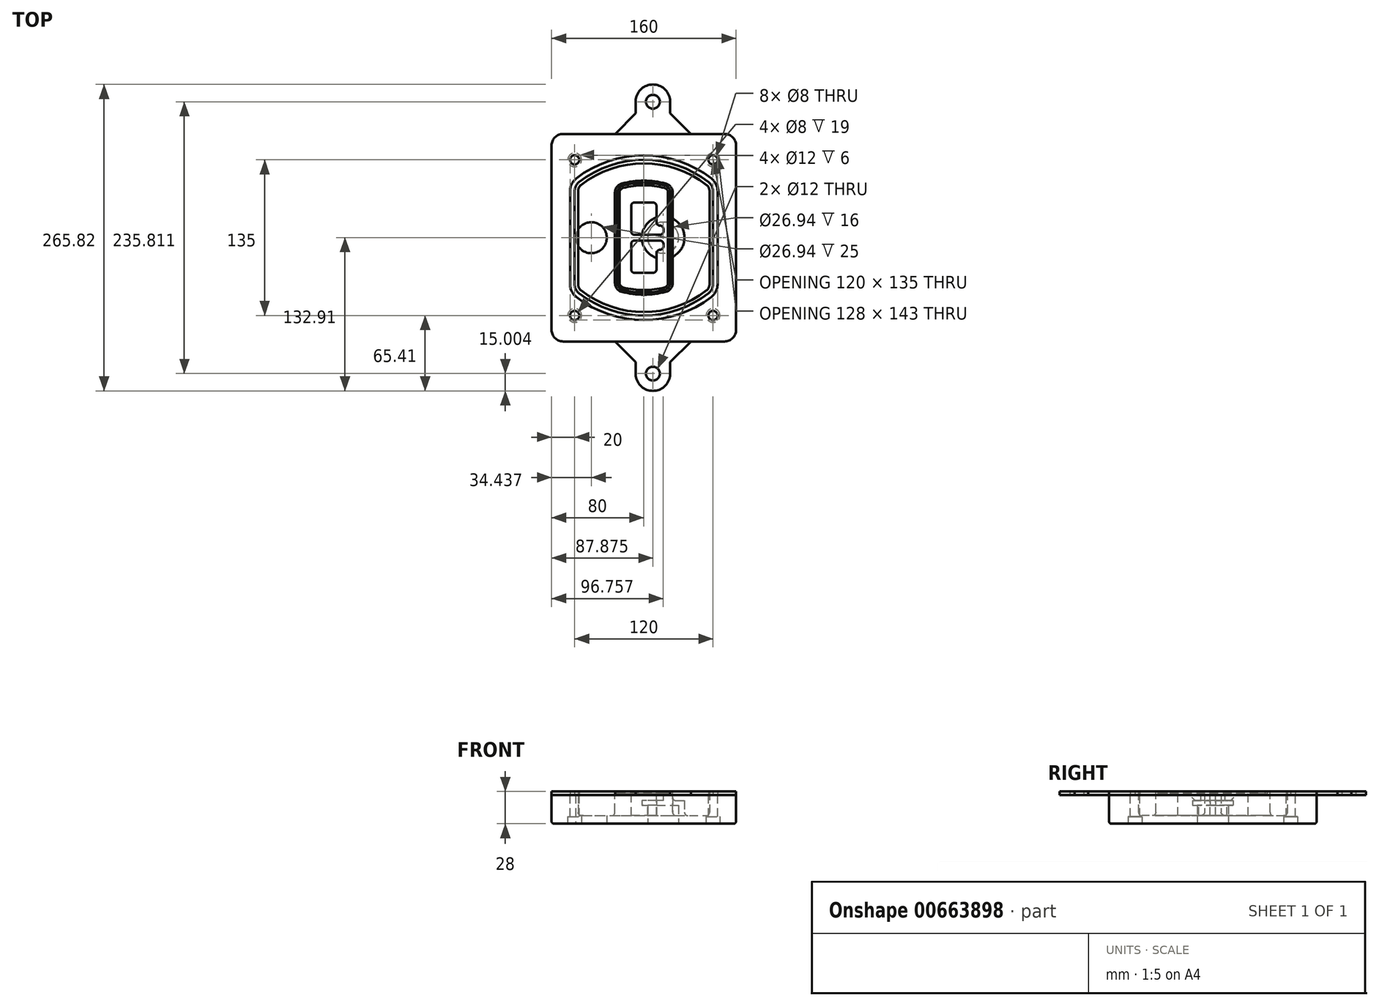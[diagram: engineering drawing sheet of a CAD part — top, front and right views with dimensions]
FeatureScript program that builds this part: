
annotation { "Feature Type Name" : "Feature", "Feature Type Description" : "" }
export const myFeature = defineFeature(function(context is Context, id is Id, definition is map)
    precondition{}
    {
        {
            var Q0;
            Q0=qCreatedBy(makeId("Top.planeOp"),FACE);
            var sketch = newSketch(context, id + "F0", { "sketchPlane" : qUnion([Q0])});
            skPoint(sketch, "E0.rect.middle", {"position": v(0, 0) * mm});
            skLineSegment(sketch, "E1.bottom", {"start": v(-70, -90) * mm, "end": v(70, -90) * mm});
            skLineSegment(sketch, "E1.top", {"start": v(-70, 90) * mm, "end": v(70, 90) * mm});
            skLineSegment(sketch, "E1.left", {"start": v(-80, -80) * mm, "end": v(-80, 80) * mm});
            skLineSegment(sketch, "E1.right", {"start": v(80, -80) * mm, "end": v(80, 80) * mm});
            skLineSegment(sketch, "E2", {"start": v(-80, 90) * mm, "end": v(80, -90) * mm, "construction": true});
            skLineSegment(sketch, "E3", {"start": v(80, 90) * mm, "end": v(-80, -90) * mm, "construction": true});
            skCircle(sketch, "E4", {"center": v(-60, 67.5) * mm, "radius": 4 * mm});
            skCircle(sketch, "E5", {"center": v(60, 67.5) * mm, "radius": 4 * mm});
            skCircle(sketch, "E6", {"center": v(60, -67.5) * mm, "radius": 4 * mm});
            skCircle(sketch, "E7", {"center": v(-60, -67.5) * mm, "radius": 4 * mm});
            skLineSegment(sketch, "E8", {"start": v(-60, 67.5) * mm, "end": v(60, 67.5) * mm, "construction": true});
            skLineSegment(sketch, "E9", {"start": v(60, 67.5) * mm, "end": v(60, -67.5) * mm, "construction": true});
            skLineSegment(sketch, "E10", {"start": v(60, -67.5) * mm, "end": v(-60, -67.5) * mm, "construction": true});
            skLineSegment(sketch, "E11", {"start": v(-60, -67.5) * mm, "end": v(-60, 67.5) * mm, "construction": true});
            skLineSegment(sketch, "E12", {"start": v(-60, 40.3) * mm, "end": v(-60, -40.3) * mm});
            skLineSegment(sketch, "E13", {"start": v(60, 40.3) * mm, "end": v(60, -40.3) * mm});
            skArc(sketch, "E14", {"start": v(56.15, 48.18) * mm, "mid": v(0, 67.5) * mm, "end": v(-56.15, 48.18) * mm});
            skArc(sketch, "E15", {"start": v(-56.15, -48.18) * mm, "mid": v(0, -67.5) * mm, "end": v(56.15, -48.18) * mm});
            skLineSegment(sketch, "E16", {"start": v(-60, 0) * mm, "end": v(60, 0) * mm, "construction": true});
            skPoint(sketch, "E17.visualSharp", {"position": v(-60, -45) * mm});
            skArc(sketch, "E17.filletArc", {"start": v(-60, -40.3) * mm, "mid": v(-58.99, -44.68) * mm, "end": v(-56.15, -48.18) * mm});
            skPoint(sketch, "E18.visualSharp", {"position": v(-60, 45) * mm});
            skArc(sketch, "E18.filletArc", {"start": v(-56.15, 48.18) * mm, "mid": v(-58.99, 44.68) * mm, "end": v(-60, 40.3) * mm});
            skPoint(sketch, "E19.visualSharp", {"position": v(60, 45) * mm});
            skArc(sketch, "E19.filletArc", {"start": v(60, 40.3) * mm, "mid": v(58.99, 44.68) * mm, "end": v(56.15, 48.18) * mm});
            skPoint(sketch, "E20.visualSharp", {"position": v(60, -45) * mm});
            skArc(sketch, "E20.filletArc", {"start": v(56.15, -48.18) * mm, "mid": v(58.99, -44.68) * mm, "end": v(60, -40.3) * mm});
            skPoint(sketch, "E21.visualSharp", {"position": v(-80, 90) * mm});
            skArc(sketch, "E21.filletArc", {"start": v(-70, 90) * mm, "mid": v(-77.07, 87.07) * mm, "end": v(-80, 80) * mm});
            skPoint(sketch, "E22.visualSharp", {"position": v(80, 90) * mm});
            skArc(sketch, "E22.filletArc", {"start": v(80, 80) * mm, "mid": v(77.07, 87.07) * mm, "end": v(70, 90) * mm});
            skPoint(sketch, "E23.visualSharp", {"position": v(80, -90) * mm});
            skArc(sketch, "E23.filletArc", {"start": v(70, -90) * mm, "mid": v(77.07, -87.07) * mm, "end": v(80, -80) * mm});
            skPoint(sketch, "E24.visualSharp", {"position": v(-80, -90) * mm});
            skArc(sketch, "E24.filletArc", {"start": v(-80, -80) * mm, "mid": v(-77.07, -87.07) * mm, "end": v(-70, -90) * mm});
            skArc(sketch, "E25.0", {"start": v(57, 40.3) * mm, "mid": v(56.3, 43.36) * mm, "end": v(54.3, 45.81) * mm});
            skLineSegment(sketch, "E25.1", {"start": v(57, 40.3) * mm, "end": v(57, -40.3) * mm});
            skArc(sketch, "E25.2", {"start": v(54.3, -45.81) * mm, "mid": v(56.3, -43.36) * mm, "end": v(57, -40.3) * mm});
            skArc(sketch, "E25.3", {"start": v(-54.3, -45.81) * mm, "mid": v(0, -64.5) * mm, "end": v(54.3, -45.81) * mm});
            skArc(sketch, "E25.4", {"start": v(-57, -40.3) * mm, "mid": v(-56.3, -43.36) * mm, "end": v(-54.3, -45.81) * mm});
            skArc(sketch, "E25.5", {"start": v(54.3, 45.81) * mm, "mid": v(0, 64.5) * mm, "end": v(-54.3, 45.81) * mm});
            skLineSegment(sketch, "E25.6", {"start": v(-57, 40.3) * mm, "end": v(-57, -40.3) * mm});
            skArc(sketch, "E25.7", {"start": v(-54.3, 45.81) * mm, "mid": v(-56.3, 43.36) * mm, "end": v(-57, 40.3) * mm});
            skArc(sketch, "E26.0", {"start": v(-58.62, 51.33) * mm, "mid": v(-62.58, 46.43) * mm, "end": v(-64, 40.3) * mm});
            skArc(sketch, "E26.1", {"start": v(58.62, 51.33) * mm, "mid": v(0, 71.5) * mm, "end": v(-58.62, 51.33) * mm});
            skArc(sketch, "E26.2", {"start": v(64, 40.3) * mm, "mid": v(62.58, 46.43) * mm, "end": v(58.62, 51.33) * mm});
            skLineSegment(sketch, "E26.3", {"start": v(64, 40.3) * mm, "end": v(64, -40.3) * mm});
            skArc(sketch, "E26.4", {"start": v(58.62, -51.33) * mm, "mid": v(62.58, -46.43) * mm, "end": v(64, -40.3) * mm});
            skLineSegment(sketch, "E26.5", {"start": v(-64, 40.3) * mm, "end": v(-64, -40.3) * mm});
            skArc(sketch, "E26.6", {"start": v(-58.62, -51.33) * mm, "mid": v(0, -71.5) * mm, "end": v(58.62, -51.33) * mm});
            skArc(sketch, "E26.7", {"start": v(-64, -40.3) * mm, "mid": v(-62.58, -46.43) * mm, "end": v(-58.62, -51.33) * mm});
            skSolve(sketch);
        }
        {
            var Q0;
            Q0=makeQuery(id+"F0.imprint","IMPRINT",FACE,{"disambiguationData":[TD([[makeQuery(id+"F0.imprint","IMPRINT",EDGE,{"derivedFrom":sQuery(id+"F0.wireOp",EDGE,"E1.bottom")}),1.0]])]});
            var Q1;
            Q1=makeQuery(id+"F0.imprint","IMPRINT",FACE,{"disambiguationData":[TD([[makeQuery(id+"F0.imprint","IMPRINT",EDGE,{"derivedFrom":sQuery(id+"F0.wireOp",EDGE,"E12")}),1.0]])]});
            var Q2;
            Q2=makeQuery(id+"F0.imprint","IMPRINT",FACE,{"disambiguationData":[TD([[makeQuery(id+"F0.imprint","IMPRINT",EDGE,{"derivedFrom":sQuery(id+"F0.wireOp",EDGE,"E25.0")}),1.0]])]});
            var Q3;
            Q3=makeQuery(id+"F0.imprint","IMPRINT",FACE,{"disambiguationData":[TD([[makeQuery(id+"F0.imprint","IMPRINT",EDGE,{"derivedFrom":sQuery(id+"F0.wireOp",EDGE,"E12")}),-1.0]])]});
            extrude(context, id + "F1", {"entities" : qUnion([Q0, Q1, Q2, Q3]), "oppositeDirection" : true, "depth" : 25 * mm});
        }
        {
            var Q0;
            Q0=makeQuery(id+"F0.imprint","IMPRINT",FACE,{"disambiguationData":[TD([[makeQuery(id+"F0.imprint","IMPRINT",EDGE,{"derivedFrom":sQuery(id+"F0.wireOp",EDGE,"E12")}),1.0]])]});
            extrude(context, id + "F2", {"entities" : qUnion([Q0]), "operationType" : NewBodyOperationType.ADD, "depth" : 3 * mm});
        }
        {
            var Q0;
            Q0=makeQuery(id+"F0.imprint","IMPRINT",FACE,{"disambiguationData":[TD([[makeQuery(id+"F0.imprint","IMPRINT",EDGE,{"derivedFrom":sQuery(id+"F0.wireOp",EDGE,"E25.0")}),1.0]])]});
            extrude(context, id + "F3", {"entities" : qUnion([Q0]), "operationType" : NewBodyOperationType.REMOVE, "oppositeDirection" : true, "depth" : 18 * mm});
        }
        {
            var Q0;
            Q0=makeQuery(id+"F2.opExtrude","CAP_FACE",FACE,{"disambiguationData":[OSD([sQuery(id+"F0.wireOp",EDGE,"E12"),sQuery(id+"F0.wireOp",EDGE,"E13"),sQuery(id+"F0.wireOp",EDGE,"E14"),sQuery(id+"F0.wireOp",EDGE,"E15"),sQuery(id+"F0.wireOp",EDGE,"E17.filletArc"),sQuery(id+"F0.wireOp",EDGE,"E18.filletArc"),sQuery(id+"F0.wireOp",EDGE,"E19.filletArc"),sQuery(id+"F0.wireOp",EDGE,"E20.filletArc"),sQuery(id+"F0.wireOp",EDGE,"E25.0"),sQuery(id+"F0.wireOp",EDGE,"E25.1"),sQuery(id+"F0.wireOp",EDGE,"E25.2"),sQuery(id+"F0.wireOp",EDGE,"E25.3"),sQuery(id+"F0.wireOp",EDGE,"E25.4"),sQuery(id+"F0.wireOp",EDGE,"E25.5"),sQuery(id+"F0.wireOp",EDGE,"E25.6"),sQuery(id+"F0.wireOp",EDGE,"E25.7")])],"isStart":false});
            var sketch = newSketch(context, id + "F4", { "sketchPlane" : qUnion([Q0])});
            skArc(sketch, "E27.0", {"start": v(-19.08, -46.97) * mm, "mid": v(0, -49.5) * mm, "end": v(19.08, -46.97) * mm});
            skArc(sketch, "E28.0", {"start": v(19.08, 46.97) * mm, "mid": v(0, 49.5) * mm, "end": v(-19.08, 46.97) * mm});
            skLineSegment(sketch, "E29", {"start": v(-25, 39.25) * mm, "end": v(-25, -39.25) * mm});
            skLineSegment(sketch, "E30", {"start": v(25, 39.25) * mm, "end": v(25, -39.25) * mm});
            skLineSegment(sketch, "E31", {"start": v(-25, 45.1) * mm, "end": v(25, 45.1) * mm, "construction": true});
            skLineSegment(sketch, "E32", {"start": v(-25, -45.1) * mm, "end": v(25, -45.1) * mm, "construction": true});
            skPoint(sketch, "E33.visualSharp", {"position": v(-25, 45.1) * mm});
            skArc(sketch, "E33.filletArc", {"start": v(-19.08, 46.97) * mm, "mid": v(-23.35, 44.11) * mm, "end": v(-25, 39.25) * mm});
            skPoint(sketch, "E34.visualSharp", {"position": v(25, 45.1) * mm});
            skArc(sketch, "E34.filletArc", {"start": v(25, 39.25) * mm, "mid": v(23.35, 44.11) * mm, "end": v(19.08, 46.97) * mm});
            skPoint(sketch, "E35.visualSharp", {"position": v(25, -45.1) * mm});
            skArc(sketch, "E35.filletArc", {"start": v(19.08, -46.97) * mm, "mid": v(23.35, -44.11) * mm, "end": v(25, -39.25) * mm});
            skPoint(sketch, "E36.visualSharp", {"position": v(-25, -45.1) * mm});
            skArc(sketch, "E36.filletArc", {"start": v(-25, -39.25) * mm, "mid": v(-23.35, -44.11) * mm, "end": v(-19.08, -46.97) * mm});
            skArc(sketch, "E37.0", {"start": v(54.3, 45.81) * mm, "mid": v(0, 64.5) * mm, "end": v(-54.3, 45.81) * mm});
            skArc(sketch, "E37.1", {"start": v(-54.3, 45.81) * mm, "mid": v(-56.3, 43.36) * mm, "end": v(-57, 40.3) * mm});
            skLineSegment(sketch, "E37.2", {"start": v(-57, 40.3) * mm, "end": v(-57, -40.3) * mm});
            skArc(sketch, "E37.3", {"start": v(-57, -40.3) * mm, "mid": v(-56.3, -43.36) * mm, "end": v(-54.3, -45.81) * mm});
            skArc(sketch, "E37.4", {"start": v(-54.3, -45.81) * mm, "mid": v(0, -64.5) * mm, "end": v(54.3, -45.81) * mm});
            skArc(sketch, "E37.5", {"start": v(54.3, -45.81) * mm, "mid": v(56.3, -43.36) * mm, "end": v(57, -40.3) * mm});
            skLineSegment(sketch, "E37.6", {"start": v(57, 40.3) * mm, "end": v(57, -40.3) * mm});
            skArc(sketch, "E37.7", {"start": v(57, 40.3) * mm, "mid": v(56.3, 43.36) * mm, "end": v(54.3, 45.81) * mm});
            skLineSegment(sketch, "E38.0", {"start": v(23, 39.25) * mm, "end": v(23, -39.25) * mm});
            skArc(sketch, "E38.1", {"start": v(18.56, -45.04) * mm, "mid": v(21.76, -42.9) * mm, "end": v(23, -39.25) * mm});
            skArc(sketch, "E38.2", {"start": v(-18.56, -45.04) * mm, "mid": v(0, -47.5) * mm, "end": v(18.56, -45.04) * mm});
            skArc(sketch, "E38.3", {"start": v(-23, -39.25) * mm, "mid": v(-21.76, -42.9) * mm, "end": v(-18.56, -45.04) * mm});
            skLineSegment(sketch, "E38.4", {"start": v(-23, 39.25) * mm, "end": v(-23, -39.25) * mm});
            skArc(sketch, "E38.5", {"start": v(23, 39.25) * mm, "mid": v(21.76, 42.9) * mm, "end": v(18.56, 45.04) * mm});
            skArc(sketch, "E38.6", {"start": v(-18.56, 45.04) * mm, "mid": v(-21.76, 42.9) * mm, "end": v(-23, 39.25) * mm});
            skArc(sketch, "E38.7", {"start": v(18.56, 45.04) * mm, "mid": v(0, 47.5) * mm, "end": v(-18.56, 45.04) * mm});
            skArc(sketch, "E39.0", {"start": v(21, 39.25) * mm, "mid": v(20.18, 41.68) * mm, "end": v(18.04, 43.1) * mm});
            skLineSegment(sketch, "E39.1", {"start": v(21, 39.25) * mm, "end": v(21, -39.25) * mm});
            skArc(sketch, "E39.2", {"start": v(18.04, -43.1) * mm, "mid": v(20.18, -41.68) * mm, "end": v(21, -39.25) * mm});
            skArc(sketch, "E39.3", {"start": v(-18.04, -43.1) * mm, "mid": v(0, -45.5) * mm, "end": v(18.04, -43.1) * mm});
            skArc(sketch, "E39.4", {"start": v(-21, -39.25) * mm, "mid": v(-20.18, -41.68) * mm, "end": v(-18.04, -43.1) * mm});
            skArc(sketch, "E39.5", {"start": v(18.04, 43.1) * mm, "mid": v(0, 45.5) * mm, "end": v(-18.04, 43.1) * mm});
            skLineSegment(sketch, "E39.6", {"start": v(-21, 39.25) * mm, "end": v(-21, -39.25) * mm});
            skArc(sketch, "E39.7", {"start": v(-18.04, 43.1) * mm, "mid": v(-20.18, 41.68) * mm, "end": v(-21, 39.25) * mm});
            skLineSegment(sketch, "E40", {"start": v(-25, 0) * mm, "end": v(25, 0) * mm, "construction": true});
            skLineSegment(sketch, "E41", {"start": v(-11, 5.5) * mm, "end": v(-11, 27.5) * mm});
            skLineSegment(sketch, "E42", {"start": v(-8, 30.5) * mm, "end": v(8, 30.5) * mm});
            skLineSegment(sketch, "E43", {"start": v(11, 27.5) * mm, "end": v(11, 13.5) * mm});
            skLineSegment(sketch, "E44", {"start": v(14, 10.5) * mm, "end": v(14, 10.5) * mm});
            skLineSegment(sketch, "E45", {"start": v(17, 7.5) * mm, "end": v(17, 5.5) * mm});
            skLineSegment(sketch, "E46", {"start": v(14, 2.5) * mm, "end": v(-8, 2.5) * mm});
            skPoint(sketch, "E47.visualSharp", {"position": v(-11, 30.5) * mm});
            skArc(sketch, "E47.filletArc", {"start": v(-8, 30.5) * mm, "mid": v(-10.12, 29.62) * mm, "end": v(-11, 27.5) * mm});
            skPoint(sketch, "E48.visualSharp", {"position": v(11, 30.5) * mm});
            skArc(sketch, "E48.filletArc", {"start": v(11, 27.5) * mm, "mid": v(10.12, 29.62) * mm, "end": v(8, 30.5) * mm});
            skPoint(sketch, "E49.visualSharp", {"position": v(11, 10.5) * mm});
            skArc(sketch, "E49.filletArc", {"start": v(11, 13.5) * mm, "mid": v(11.88, 11.38) * mm, "end": v(14, 10.5) * mm});
            skPoint(sketch, "E50.visualSharp", {"position": v(17, 10.5) * mm});
            skArc(sketch, "E50.filletArc", {"start": v(17, 7.5) * mm, "mid": v(16.12, 9.62) * mm, "end": v(14, 10.5) * mm});
            skPoint(sketch, "E51.visualSharp", {"position": v(17, 2.5) * mm});
            skArc(sketch, "E51.filletArc", {"start": v(14, 2.5) * mm, "mid": v(16.12, 3.38) * mm, "end": v(17, 5.5) * mm});
            skPoint(sketch, "E52.visualSharp", {"position": v(-11, 2.5) * mm});
            skArc(sketch, "E52.filletArc", {"start": v(-11, 5.5) * mm, "mid": v(-10.12, 3.38) * mm, "end": v(-8, 2.5) * mm});
            skLineSegment(sketch, "E53.0.MirrorCS", {"start": v(14, -2.5) * mm, "end": v(-8, -2.5) * mm});
            skArc(sketch, "E54.0.MirrorCS", {"start": v(-11, -5.5) * mm, "mid": v(-10.12, -3.38) * mm, "end": v(-8, -2.5) * mm});
            skLineSegment(sketch, "E55.0.MirrorCS", {"start": v(-11, -5.5) * mm, "end": v(-11, -27.5) * mm});
            skArc(sketch, "E56.0.MirrorCS", {"start": v(-8, -30.5) * mm, "mid": v(-10.12, -29.62) * mm, "end": v(-11, -27.5) * mm});
            skLineSegment(sketch, "E57.0.MirrorCS", {"start": v(-8, -30.5) * mm, "end": v(8, -30.5) * mm});
            skArc(sketch, "E58.0.MirrorCS", {"start": v(11, -27.5) * mm, "mid": v(10.12, -29.62) * mm, "end": v(8, -30.5) * mm});
            skLineSegment(sketch, "E59.0.MirrorCS", {"start": v(11, -27.5) * mm, "end": v(11, -13.5) * mm});
            skArc(sketch, "E60.0.MirrorCS", {"start": v(11, -13.5) * mm, "mid": v(11.88, -11.38) * mm, "end": v(14, -10.5) * mm});
            skArc(sketch, "E61.0.MirrorCS", {"start": v(17, -7.5) * mm, "mid": v(16.12, -9.62) * mm, "end": v(14, -10.5) * mm});
            skLineSegment(sketch, "E62.0.MirrorCS", {"start": v(17, -7.5) * mm, "end": v(17, -5.5) * mm});
            skArc(sketch, "E63.0.MirrorCS", {"start": v(14, -2.5) * mm, "mid": v(16.12, -3.38) * mm, "end": v(17, -5.5) * mm});
            skSolve(sketch);
        }
        {
            var Q0;
            Q0=makeQuery(id+"F4.imprint","IMPRINT",FACE,{"disambiguationData":[TD([[makeQuery(id+"F4.imprint","IMPRINT",EDGE,{"derivedFrom":sQuery(id+"F4.wireOp",EDGE,"E27.0")}),1.0]])]});
            var Q1;
            Q1=makeQuery(id+"F4.imprint","IMPRINT",FACE,{"disambiguationData":[TD([[makeQuery(id+"F4.imprint","IMPRINT",EDGE,{"derivedFrom":sQuery(id+"F4.wireOp",EDGE,"E38.0")}),-1.0]])]});
            var Q2;
            Q2=makeQuery(id+"F4.imprint","IMPRINT",FACE,{"disambiguationData":[TD([[makeQuery(id+"F4.imprint","IMPRINT",EDGE,{"derivedFrom":sQuery(id+"F4.wireOp",EDGE,"E39.0")}),1.0]])]});
            extrude(context, id + "F5", {"entities" : qUnion([Q0, Q1, Q2]), "operationType" : NewBodyOperationType.ADD, "endBound" : BoundingType.UP_TO_NEXT, "oppositeDirection" : true, "depth" : 25 * mm});
        }
        {
            var Q0;
            Q0=makeQuery(id+"F4.imprint","IMPRINT",FACE,{"disambiguationData":[TD([[makeQuery(id+"F4.imprint","IMPRINT",EDGE,{"derivedFrom":sQuery(id+"F4.wireOp",EDGE,"E38.0")}),-1.0]])]});
            extrude(context, id + "F6", {"entities" : qUnion([Q0]), "operationType" : NewBodyOperationType.REMOVE, "oppositeDirection" : true, "depth" : 2 * mm});
        }
        {
            var Q0;
            Q0=makeQuery(id+"F1.opExtrude","CAP_FACE",FACE,{"disambiguationData":[OSD([sQuery(id+"F0.wireOp",EDGE,"E1.bottom"),sQuery(id+"F0.wireOp",EDGE,"E1.top"),sQuery(id+"F0.wireOp",EDGE,"E1.left"),sQuery(id+"F0.wireOp",EDGE,"E1.right"),sQuery(id+"F0.wireOp",EDGE,"E4"),sQuery(id+"F0.wireOp",EDGE,"E5"),sQuery(id+"F0.wireOp",EDGE,"E6"),sQuery(id+"F0.wireOp",EDGE,"E7"),sQuery(id+"F0.wireOp",EDGE,"E21.filletArc"),sQuery(id+"F0.wireOp",EDGE,"E22.filletArc"),sQuery(id+"F0.wireOp",EDGE,"E23.filletArc"),sQuery(id+"F0.wireOp",EDGE,"E24.filletArc")])],"isStart":false});
            var sketch = newSketch(context, id + "F7", { "sketchPlane" : qUnion([Q0])});
            skCircle(sketch, "E64", {"center": v(16.76, 0) * mm, "radius": 13.47 * mm});
            skCircle(sketch, "E65", {"center": v(-45.56, 0) * mm, "radius": 13.47 * mm});
            skLineSegment(sketch, "E66", {"start": v(80, 0) * mm, "end": v(-80, 0) * mm});
            skCircle(sketch, "E67", {"center": v(16.76, 0) * mm, "radius": 18.47 * mm});
            skCircle(sketch, "E68", {"center": v(60, -67.5) * mm, "radius": 6 * mm});
            skCircle(sketch, "E69", {"center": v(-60, -67.5) * mm, "radius": 6 * mm});
            skCircle(sketch, "E70", {"center": v(-60, 67.5) * mm, "radius": 6 * mm});
            skCircle(sketch, "E71", {"center": v(60, 67.5) * mm, "radius": 6 * mm});
            skSolve(sketch);
        }
        {
            var Q0;
            {var subQ1=sQuery(id+"F7.wireOp",EDGE,"E66");var subQ4=sQuery(id+"F7.wireOp",EDGE,"E64");var subQ6=makeQuery(id+"F7.imprint","INTERSECT",VERTEX,{"disambiguationData":[OD(0.0)],"derivedFrom":[subQ4,subQ1]});Q0=makeQuery(id+"F7.imprint","IMPRINT",FACE,{"disambiguationData":[TD([[makeQuery(id+"F7.imprint","IMPRINT",EDGE,{"disambiguationData":[TD([[subQ6,-1.0]])],"derivedFrom":subQ4}),-1.0]])]});}
            var Q1;
            {var subQ0=sQuery(id+"F7.wireOp",EDGE,"E66");var subQ1=sQuery(id+"F7.wireOp",EDGE,"E64");var subQ3=makeQuery(id+"F7.imprint","INTERSECT",VERTEX,{"disambiguationData":[OD(0.0)],"derivedFrom":[subQ1,subQ0]});Q1=makeQuery(id+"F7.imprint","IMPRINT",FACE,{"disambiguationData":[TD([[makeQuery(id+"F7.imprint","IMPRINT",EDGE,{"disambiguationData":[TD([[subQ3,-1.0]])],"derivedFrom":subQ1}),1.0]])]});}
            var Q2;
            {var subQ0=sQuery(id+"F7.wireOp",EDGE,"E66");var subQ1=sQuery(id+"F7.wireOp",EDGE,"E64");var subQ3=makeQuery(id+"F7.imprint","INTERSECT",VERTEX,{"disambiguationData":[OD(0.0)],"derivedFrom":[subQ1,subQ0]});Q2=makeQuery(id+"F7.imprint","IMPRINT",FACE,{"disambiguationData":[TD([[makeQuery(id+"F7.imprint","IMPRINT",EDGE,{"disambiguationData":[TD([[subQ3,1.0]])],"derivedFrom":subQ1}),1.0]])]});}
            var Q3;
            {var subQ1=sQuery(id+"F7.wireOp",EDGE,"E66");var subQ4=sQuery(id+"F7.wireOp",EDGE,"E64");var subQ6=makeQuery(id+"F7.imprint","INTERSECT",VERTEX,{"disambiguationData":[OD(0.0)],"derivedFrom":[subQ4,subQ1]});Q3=makeQuery(id+"F7.imprint","IMPRINT",FACE,{"disambiguationData":[TD([[makeQuery(id+"F7.imprint","IMPRINT",EDGE,{"disambiguationData":[TD([[subQ6,1.0]])],"derivedFrom":subQ4}),-1.0]])]});}
            extrude(context, id + "F8", {"entities" : qUnion([Q0, Q1, Q2, Q3]), "operationType" : NewBodyOperationType.ADD, "oppositeDirection" : true, "depth" : 20 * mm});
        }
        {
            var Q0;
            {var subQ0=sQuery(id+"F7.wireOp",EDGE,"E66");var subQ1=sQuery(id+"F7.wireOp",EDGE,"E64");var subQ3=makeQuery(id+"F7.imprint","INTERSECT",VERTEX,{"disambiguationData":[OD(0.0)],"derivedFrom":[subQ1,subQ0]});Q0=makeQuery(id+"F7.imprint","IMPRINT",FACE,{"disambiguationData":[TD([[makeQuery(id+"F7.imprint","IMPRINT",EDGE,{"disambiguationData":[TD([[subQ3,-1.0]])],"derivedFrom":subQ1}),1.0]])]});}
            var Q1;
            {var subQ0=sQuery(id+"F7.wireOp",EDGE,"E66");var subQ1=sQuery(id+"F7.wireOp",EDGE,"E64");var subQ3=makeQuery(id+"F7.imprint","INTERSECT",VERTEX,{"disambiguationData":[OD(0.0)],"derivedFrom":[subQ1,subQ0]});Q1=makeQuery(id+"F7.imprint","IMPRINT",FACE,{"disambiguationData":[TD([[makeQuery(id+"F7.imprint","IMPRINT",EDGE,{"disambiguationData":[TD([[subQ3,1.0]])],"derivedFrom":subQ1}),1.0]])]});}
            extrude(context, id + "F9", {"entities" : qUnion([Q0, Q1]), "operationType" : NewBodyOperationType.REMOVE, "oppositeDirection" : true, "depth" : 16 * mm});
        }
        {
            var Q0;
            {var subQ0=sQuery(id+"F7.wireOp",EDGE,"E66");var subQ1=sQuery(id+"F7.wireOp",EDGE,"E65");var subQ3=makeQuery(id+"F7.imprint","INTERSECT",VERTEX,{"disambiguationData":[OD(0.0)],"derivedFrom":[subQ1,subQ0]});Q0=makeQuery(id+"F7.imprint","IMPRINT",FACE,{"disambiguationData":[TD([[makeQuery(id+"F7.imprint","IMPRINT",EDGE,{"disambiguationData":[TD([[subQ3,-1.0]])],"derivedFrom":subQ1}),1.0]])]});}
            var Q1;
            {var subQ0=sQuery(id+"F7.wireOp",EDGE,"E66");var subQ1=sQuery(id+"F7.wireOp",EDGE,"E65");var subQ3=makeQuery(id+"F7.imprint","INTERSECT",VERTEX,{"disambiguationData":[OD(0.0)],"derivedFrom":[subQ1,subQ0]});Q1=makeQuery(id+"F7.imprint","IMPRINT",FACE,{"disambiguationData":[TD([[makeQuery(id+"F7.imprint","IMPRINT",EDGE,{"disambiguationData":[TD([[subQ3,1.0]])],"derivedFrom":subQ1}),1.0]])]});}
            extrude(context, id + "F10", {"entities" : qUnion([Q0, Q1]), "operationType" : NewBodyOperationType.REMOVE, "oppositeDirection" : true, "depth" : 25 * mm});
        }
        {
            var Q0;
            Q0=makeQuery(id+"F7.imprint","IMPRINT",FACE,{"disambiguationData":[TD([[makeQuery(id+"F7.imprint","IMPRINT",EDGE,{"derivedFrom":sQuery(id+"F7.wireOp",EDGE,"E68")}),1.0]])]});
            var Q1;
            Q1=makeQuery(id+"F7.imprint","IMPRINT",FACE,{"disambiguationData":[TD([[makeQuery(id+"F7.imprint","IMPRINT",EDGE,{"derivedFrom":makeQuery(id+"F1.opExtrude","CAP_EDGE",EDGE,{"disambiguationData":[OSD([sQuery(id+"F0.wireOp",EDGE,"E5")])],"isStart":false})}),-1.0]])]});
            var Q2;
            Q2=makeQuery(id+"F7.imprint","IMPRINT",FACE,{"disambiguationData":[TD([[makeQuery(id+"F7.imprint","IMPRINT",EDGE,{"derivedFrom":sQuery(id+"F7.wireOp",EDGE,"E69")}),1.0]])]});
            var Q3;
            Q3=makeQuery(id+"F7.imprint","IMPRINT",FACE,{"disambiguationData":[TD([[makeQuery(id+"F7.imprint","IMPRINT",EDGE,{"derivedFrom":makeQuery(id+"F1.opExtrude","CAP_EDGE",EDGE,{"disambiguationData":[OSD([sQuery(id+"F0.wireOp",EDGE,"E4")])],"isStart":false})}),-1.0]])]});
            var Q4;
            Q4=makeQuery(id+"F7.imprint","IMPRINT",FACE,{"disambiguationData":[TD([[makeQuery(id+"F7.imprint","IMPRINT",EDGE,{"derivedFrom":sQuery(id+"F7.wireOp",EDGE,"E70")}),1.0]])]});
            var Q5;
            Q5=makeQuery(id+"F7.imprint","IMPRINT",FACE,{"disambiguationData":[TD([[makeQuery(id+"F7.imprint","IMPRINT",EDGE,{"derivedFrom":makeQuery(id+"F1.opExtrude","CAP_EDGE",EDGE,{"disambiguationData":[OSD([sQuery(id+"F0.wireOp",EDGE,"E7")])],"isStart":false})}),-1.0]])]});
            var Q6;
            Q6=makeQuery(id+"F7.imprint","IMPRINT",FACE,{"disambiguationData":[TD([[makeQuery(id+"F7.imprint","IMPRINT",EDGE,{"derivedFrom":sQuery(id+"F7.wireOp",EDGE,"E71")}),1.0]])]});
            var Q7;
            Q7=makeQuery(id+"F7.imprint","IMPRINT",FACE,{"disambiguationData":[TD([[makeQuery(id+"F7.imprint","IMPRINT",EDGE,{"derivedFrom":makeQuery(id+"F1.opExtrude","CAP_EDGE",EDGE,{"disambiguationData":[OSD([sQuery(id+"F0.wireOp",EDGE,"E6")])],"isStart":false})}),-1.0]])]});
            extrude(context, id + "F11", {"entities" : qUnion([Q0, Q1, Q2, Q3, Q4, Q5, Q6, Q7]), "operationType" : NewBodyOperationType.REMOVE, "oppositeDirection" : true, "depth" : 6 * mm});
        }
        {
            var Q0;
            Q0=makeQuery(id+"F9.boolean.opBoolean","COPY",FACE,{"derivedFrom":makeQuery(id+"F9.opExtrude","CAP_FACE",FACE,{"disambiguationData":[OSD([sQuery(id+"F7.wireOp",EDGE,"E64")])],"isStart":false})});
            var sketch = newSketch(context, id + "F12", { "sketchPlane" : qUnion([Q0])});
            skArc(sketch, "E72.0", {"start": v(11, 17.55) * mm, "mid": v(2.57, 11.82) * mm, "end": v(-1.54, 2.5) * mm});
            skArc(sketch, "E72.1", {"start": v(-1.54, -2.5) * mm, "mid": v(2.57, -11.82) * mm, "end": v(11, -17.55) * mm});
            skLineSegment(sketch, "E73", {"start": v(-1.54, -2.5) * mm, "end": v(14, -2.5) * mm});
            skLineSegment(sketch, "E74.0", {"start": v(14, 2.5) * mm, "end": v(-1.54, 2.5) * mm});
            skArc(sketch, "E74.1", {"start": v(14, 2.5) * mm, "mid": v(16.12, 3.38) * mm, "end": v(17, 5.5) * mm});
            skLineSegment(sketch, "E74.2", {"start": v(17, 7.5) * mm, "end": v(17, 5.5) * mm});
            skArc(sketch, "E74.3", {"start": v(17, 7.5) * mm, "mid": v(16.12, 9.62) * mm, "end": v(14, 10.5) * mm});
            skArc(sketch, "E74.4", {"start": v(11, 13.5) * mm, "mid": v(11.88, 11.38) * mm, "end": v(14, 10.5) * mm});
            skLineSegment(sketch, "E74.5", {"start": v(11, 17.55) * mm, "end": v(11, 13.5) * mm});
            skLineSegment(sketch, "E74.7", {"start": v(14, -2.5) * mm, "end": v(-1.54, -2.5) * mm});
            skArc(sketch, "E74.8", {"start": v(14, -2.5) * mm, "mid": v(16.12, -3.38) * mm, "end": v(17, -5.5) * mm});
            skLineSegment(sketch, "E74.9", {"start": v(17, -7.5) * mm, "end": v(17, -5.5) * mm});
            skArc(sketch, "E74.10", {"start": v(17, -7.5) * mm, "mid": v(16.12, -9.62) * mm, "end": v(14, -10.5) * mm});
            skArc(sketch, "E74.11", {"start": v(11, -13.5) * mm, "mid": v(11.88, -11.38) * mm, "end": v(14, -10.5) * mm});
            skLineSegment(sketch, "E74.12", {"start": v(11, -17.55) * mm, "end": v(11, -13.5) * mm});
            skPoint(sketch, "E75.orphan", {"position": v(11, -27.5) * mm});
            skPoint(sketch, "E76.orphan", {"position": v(-8, -2.5) * mm});
            skPoint(sketch, "E77.orphan", {"position": v(-8, 2.5) * mm});
            skPoint(sketch, "E78.orphan", {"position": v(11, 27.5) * mm});
            skSolve(sketch);
        }
        {
            var Q0;
            {var subQ7=sQuery(id+"F12.wireOp",EDGE,"E72.0");var subQ14=sQuery(id+"F12.wireOp",EDGE,"E72.1");var subQ16=sQuery(id+"F12.wireOp",EDGE,"E74.1");var subQ18=sQuery(id+"F12.wireOp",EDGE,"E74.8");Q0=qUnion([makeQuery(id+"F12.imprint","IMPRINT",FACE,{"disambiguationData":[TD([[makeQuery(id+"F12.imprint","IMPRINT",EDGE,{"derivedFrom":subQ7}),1.0]])]}),makeQuery(id+"F12.imprint","IMPRINT",FACE,{"disambiguationData":[TD([[makeQuery(id+"F12.imprint","IMPRINT",EDGE,{"derivedFrom":subQ14}),1.0]])]}),makeQuery(id+"F12.imprint","IMPRINT",FACE,{"disambiguationData":[TD([[makeQuery(id+"F12.imprint","IMPRINT",EDGE,{"derivedFrom":subQ16}),1.0]])]}),makeQuery(id+"F12.imprint","IMPRINT",FACE,{"disambiguationData":[TD([[makeQuery(id+"F12.imprint","IMPRINT",EDGE,{"derivedFrom":subQ18}),-1.0]])]})]);}
            var Q1;
            Q1=makeQuery(id+"F5.boolean.opBoolean","SPLIT",FACE,{"disambiguationData":[TD([makeQuery(id+"F5.opExtrude","SWEPT_FACE",FACE,{"disambiguationData":[OSD([sQuery(id+"F4.wireOp",EDGE,"E41")])]})])],"derivedFrom":makeQuery(id+"F3.boolean.opBoolean","COPY",FACE,{"derivedFrom":makeQuery(id+"F3.opExtrude","CAP_FACE",FACE,{"disambiguationData":[OSD([sQuery(id+"F0.wireOp",EDGE,"E25.0"),sQuery(id+"F0.wireOp",EDGE,"E25.1"),sQuery(id+"F0.wireOp",EDGE,"E25.2"),sQuery(id+"F0.wireOp",EDGE,"E25.3"),sQuery(id+"F0.wireOp",EDGE,"E25.4"),sQuery(id+"F0.wireOp",EDGE,"E25.5"),sQuery(id+"F0.wireOp",EDGE,"E25.6"),sQuery(id+"F0.wireOp",EDGE,"E25.7")])],"isStart":false})})});
            extrude(context, id + "F13", {"entities" : qUnion([Q0]), "operationType" : NewBodyOperationType.REMOVE, "endBound" : BoundingType.UP_TO_SURFACE, "endBoundEntityFace" : qUnion([Q1]), "depth" : 25 * mm});
        }
        {
            var Q0;
            Q0=makeQuery(id+"F3.boolean.opBoolean","COPY",EDGE,{"derivedFrom":makeQuery(id+"F3.opExtrude","CAP_EDGE",EDGE,{"disambiguationData":[OSD([sQuery(id+"F0.wireOp",EDGE,"E25.6")])],"isStart":false})});
            var Q1;
            Q1=makeQuery(id+"F8.boolean.opBoolean","INTERSECT",EDGE,{"derivedFrom":[makeQuery(id+"F5.opExtrude","SWEPT_FACE",FACE,{"disambiguationData":[OSD([sQuery(id+"F4.wireOp",EDGE,"E30")])]}),makeQuery(id+"F8.opExtrude","CAP_FACE",FACE,{"disambiguationData":[OSD([sQuery(id+"F7.wireOp",EDGE,"E67")])],"isStart":false})]});
            var Q2;
            Q2=makeQuery(id+"F8.boolean.opBoolean","INTERSECT",EDGE,{"disambiguationData":[OD(1.0)],"derivedFrom":[makeQuery(id+"F5.opExtrude","SWEPT_FACE",FACE,{"disambiguationData":[OSD([sQuery(id+"F4.wireOp",EDGE,"E30")])]}),makeQuery(id+"F8.opExtrude","SWEPT_FACE",FACE,{"disambiguationData":[OSD([sQuery(id+"F7.wireOp",EDGE,"E67")])]})]});
            var Q3;
            {var subQ0=sQuery(id+"F4.wireOp",EDGE,"E30");Q3=makeQuery(id+"F8.boolean.opBoolean","SPLIT",EDGE,{"disambiguationData":[TD([makeQuery(id+"F5.opExtrude","SWEPT_FACE",FACE,{"disambiguationData":[OSD([sQuery(id+"F4.wireOp",EDGE,"E35.filletArc")])]})])],"derivedFrom":makeQuery(id+"F5.opExtrude","CAP_EDGE",EDGE,{"disambiguationData":[OSD([subQ0])],"isStart":false})});}
            var Q4;
            {var subQ0=sQuery(id+"F0.wireOp",EDGE,"E25.7");var subQ1=sQuery(id+"F0.wireOp",EDGE,"E25.1");var subQ2=sQuery(id+"F0.wireOp",EDGE,"E25.6");var subQ3=sQuery(id+"F0.wireOp",EDGE,"E25.5");var subQ4=sQuery(id+"F0.wireOp",EDGE,"E25.4");var subQ5=sQuery(id+"F0.wireOp",EDGE,"E25.0");var subQ6=sQuery(id+"F0.wireOp",EDGE,"E25.2");var subQ7=sQuery(id+"F0.wireOp",EDGE,"E25.3");Q4=makeQuery(id+"F8.boolean.opBoolean","INTERSECT",EDGE,{"derivedFrom":[makeQuery(id+"F5.boolean.opBoolean","SPLIT",FACE,{"disambiguationData":[TD([makeQuery(id+"F2.opExtrude","SWEPT_FACE",FACE,{"disambiguationData":[OSD([subQ5])]})])],"derivedFrom":makeQuery(id+"F3.boolean.opBoolean","COPY",FACE,{"derivedFrom":makeQuery(id+"F3.opExtrude","CAP_FACE",FACE,{"disambiguationData":[OSD([subQ5,subQ1,subQ6,subQ7,subQ4,subQ3,subQ2,subQ0])],"isStart":false})})}),makeQuery(id+"F8.opExtrude","SWEPT_FACE",FACE,{"disambiguationData":[OSD([sQuery(id+"F7.wireOp",EDGE,"E67")])]})]});}
            var Q5;
            Q5=makeQuery(id+"F8.boolean.opBoolean","INTERSECT",EDGE,{"disambiguationData":[OD(0.0)],"derivedFrom":[makeQuery(id+"F5.opExtrude","SWEPT_FACE",FACE,{"disambiguationData":[OSD([sQuery(id+"F4.wireOp",EDGE,"E30")])]}),makeQuery(id+"F8.opExtrude","SWEPT_FACE",FACE,{"disambiguationData":[OSD([sQuery(id+"F7.wireOp",EDGE,"E67")])]})]});
            fillet(context, id + "F14", {"entities" : qUnion([Q0, Q1, Q2, Q3, Q4, Q5]), "radius" : 3 * mm, "tangentPropagation" : true, "allowEdgeOverflow" : false});
        }
        {
            var Q0;
            Q0=makeQuery(id+"F1.opExtrude","CAP_EDGE",EDGE,{"disambiguationData":[OSD([sQuery(id+"F0.wireOp",EDGE,"E1.bottom")])],"isStart":false});
            fillet(context, id + "F15", {"entities" : qUnion([Q0]), "radius" : 2 * mm, "tangentPropagation" : true, "allowEdgeOverflow" : false});
        }
        {
            var Q0;
            {var subQ0=sQuery(id+"F0.wireOp",EDGE,"E21.filletArc");var subQ1=sQuery(id+"F0.wireOp",EDGE,"E7");var subQ2=sQuery(id+"F0.wireOp",EDGE,"E6");var subQ3=sQuery(id+"F0.wireOp",EDGE,"E5");var subQ4=sQuery(id+"F0.wireOp",EDGE,"E4");var subQ5=sQuery(id+"F0.wireOp",EDGE,"E22.filletArc");var subQ6=sQuery(id+"F0.wireOp",EDGE,"E1.bottom");var subQ7=sQuery(id+"F0.wireOp",EDGE,"E1.right");var subQ8=sQuery(id+"F0.wireOp",EDGE,"E1.top");var subQ9=sQuery(id+"F0.wireOp",EDGE,"E1.left");var subQ10=sQuery(id+"F0.wireOp",EDGE,"E23.filletArc");var subQ11=sQuery(id+"F0.wireOp",EDGE,"E24.filletArc");Q0=makeQuery(id+"F2.boolean.opBoolean","SPLIT",FACE,{"disambiguationData":[TD([makeQuery(id+"F1.opExtrude","SWEPT_FACE",FACE,{"disambiguationData":[OSD([subQ6])]})])],"derivedFrom":makeQuery(id+"F1.opExtrude","CAP_FACE",FACE,{"disambiguationData":[OSD([subQ6,subQ8,subQ9,subQ7,subQ4,subQ3,subQ2,subQ1,subQ0,subQ5,subQ10,subQ11])],"isStart":true})});}
            var sketch = newSketch(context, id + "F16", { "sketchPlane" : qUnion([Q0])});
            skLineSegment(sketch, "E79", {"start": v(-24.98, 90) * mm, "end": v(-6.98, 108) * mm});
            skLineSegment(sketch, "E80", {"start": v(40.73, 90) * mm, "end": v(22.73, 108) * mm});
            skLineSegment(sketch, "E81", {"start": v(-6.98, 108) * mm, "end": v(-6.98, 120) * mm});
            skLineSegment(sketch, "E82", {"start": v(22.73, 108) * mm, "end": v(22.73, 120) * mm});
            skArc(sketch, "E83", {"start": v(22.73, 120) * mm, "mid": v(7.88, 132.9) * mm, "end": v(-6.98, 120) * mm});
            skCircle(sketch, "E84", {"center": v(7.88, 117.9) * mm, "radius": 6 * mm});
            skLineSegment(sketch, "E85", {"start": v(80, 0) * mm, "end": v(-80, 0) * mm, "construction": true});
            skLineSegment(sketch, "E86.MirrorCS", {"start": v(40.73, -90) * mm, "end": v(22.73, -108) * mm});
            skLineSegment(sketch, "E87.MirrorCS", {"start": v(22.73, -108) * mm, "end": v(22.73, -120) * mm});
            skLineSegment(sketch, "E88.MirrorCS", {"start": v(-6.98, -108) * mm, "end": v(-6.98, -120) * mm});
            skCircle(sketch, "E89.MirrorC", {"center": v(7.88, -117.9) * mm, "radius": 6 * mm});
            skArc(sketch, "E90.MirrorCS", {"start": v(22.73, -120) * mm, "mid": v(7.88, -132.9) * mm, "end": v(-6.98, -120) * mm});
            skLineSegment(sketch, "E91.MirrorCS", {"start": v(-24.98, -90) * mm, "end": v(-6.98, -108) * mm});
            skSolve(sketch);
        }
        {
            var Q0;
            {var subQ0=sQuery(id+"F16.wireOp",EDGE,"E79");Q0=makeQuery(id+"F16.imprint","IMPRINT",FACE,{"disambiguationData":[TD([[makeQuery(id+"F16.imprint","IMPRINT",EDGE,{"derivedFrom":subQ0}),-1.0]])]});}
            var Q1;
            Q1=makeQuery(id+"F16.imprint","IMPRINT",FACE,{"disambiguationData":[TD([[makeQuery(id+"F16.imprint","IMPRINT",EDGE,{"derivedFrom":makeQuery(id+"F1.opExtrude","CAP_EDGE",EDGE,{"disambiguationData":[OSD([sQuery(id+"F0.wireOp",EDGE,"E1.left")])],"isStart":true})}),-1.0]])]});
            var Q2;
            {var subQ0=sQuery(id+"F16.wireOp",EDGE,"E86.MirrorCS");Q2=makeQuery(id+"F16.imprint","IMPRINT",FACE,{"disambiguationData":[TD([[makeQuery(id+"F16.imprint","IMPRINT",EDGE,{"derivedFrom":subQ0}),-1.0]])]});}
            var Q3;
            Q3=makeQuery(id+"F2.opExtrude","CAP_FACE",FACE,{"disambiguationData":[OSD([sQuery(id+"F0.wireOp",EDGE,"E12"),sQuery(id+"F0.wireOp",EDGE,"E13"),sQuery(id+"F0.wireOp",EDGE,"E14"),sQuery(id+"F0.wireOp",EDGE,"E15"),sQuery(id+"F0.wireOp",EDGE,"E17.filletArc"),sQuery(id+"F0.wireOp",EDGE,"E18.filletArc"),sQuery(id+"F0.wireOp",EDGE,"E19.filletArc"),sQuery(id+"F0.wireOp",EDGE,"E20.filletArc"),sQuery(id+"F0.wireOp",EDGE,"E25.0"),sQuery(id+"F0.wireOp",EDGE,"E25.1"),sQuery(id+"F0.wireOp",EDGE,"E25.2"),sQuery(id+"F0.wireOp",EDGE,"E25.3"),sQuery(id+"F0.wireOp",EDGE,"E25.4"),sQuery(id+"F0.wireOp",EDGE,"E25.5"),sQuery(id+"F0.wireOp",EDGE,"E25.6"),sQuery(id+"F0.wireOp",EDGE,"E25.7")])],"isStart":false});
            extrude(context, id + "F17", {"entities" : qUnion([Q0, Q1, Q2]), "endBound" : BoundingType.UP_TO_SURFACE, "depth" : 25.4 * mm, "endBoundEntityFace" : qUnion([Q3]), "offsetDistance" : 25.4 * mm});
        }
        {
            var Q0;
            Q0 = qSketchRegion(id + "F0", true);
            var Q1;
            Q1=makeQuery(id+"F2.opExtrude","CAP_FACE",FACE,{"disambiguationData":[OSD([sQuery(id+"F0.wireOp",EDGE,"E12"),sQuery(id+"F0.wireOp",EDGE,"E13"),sQuery(id+"F0.wireOp",EDGE,"E14"),sQuery(id+"F0.wireOp",EDGE,"E15"),sQuery(id+"F0.wireOp",EDGE,"E17.filletArc"),sQuery(id+"F0.wireOp",EDGE,"E18.filletArc"),sQuery(id+"F0.wireOp",EDGE,"E19.filletArc"),sQuery(id+"F0.wireOp",EDGE,"E20.filletArc"),sQuery(id+"F0.wireOp",EDGE,"E25.0"),sQuery(id+"F0.wireOp",EDGE,"E25.1"),sQuery(id+"F0.wireOp",EDGE,"E25.2"),sQuery(id+"F0.wireOp",EDGE,"E25.3"),sQuery(id+"F0.wireOp",EDGE,"E25.4"),sQuery(id+"F0.wireOp",EDGE,"E25.5"),sQuery(id+"F0.wireOp",EDGE,"E25.6"),sQuery(id+"F0.wireOp",EDGE,"E25.7")])],"isStart":false});
            extrude(context, id + "F18", {"entities" : qUnion([Q0]), "endBound" : BoundingType.UP_TO_SURFACE, "depth" : 25 * mm, "endBoundEntityFace" : qUnion([Q1]), "offsetDistance" : 25 * mm});
        }
    });
